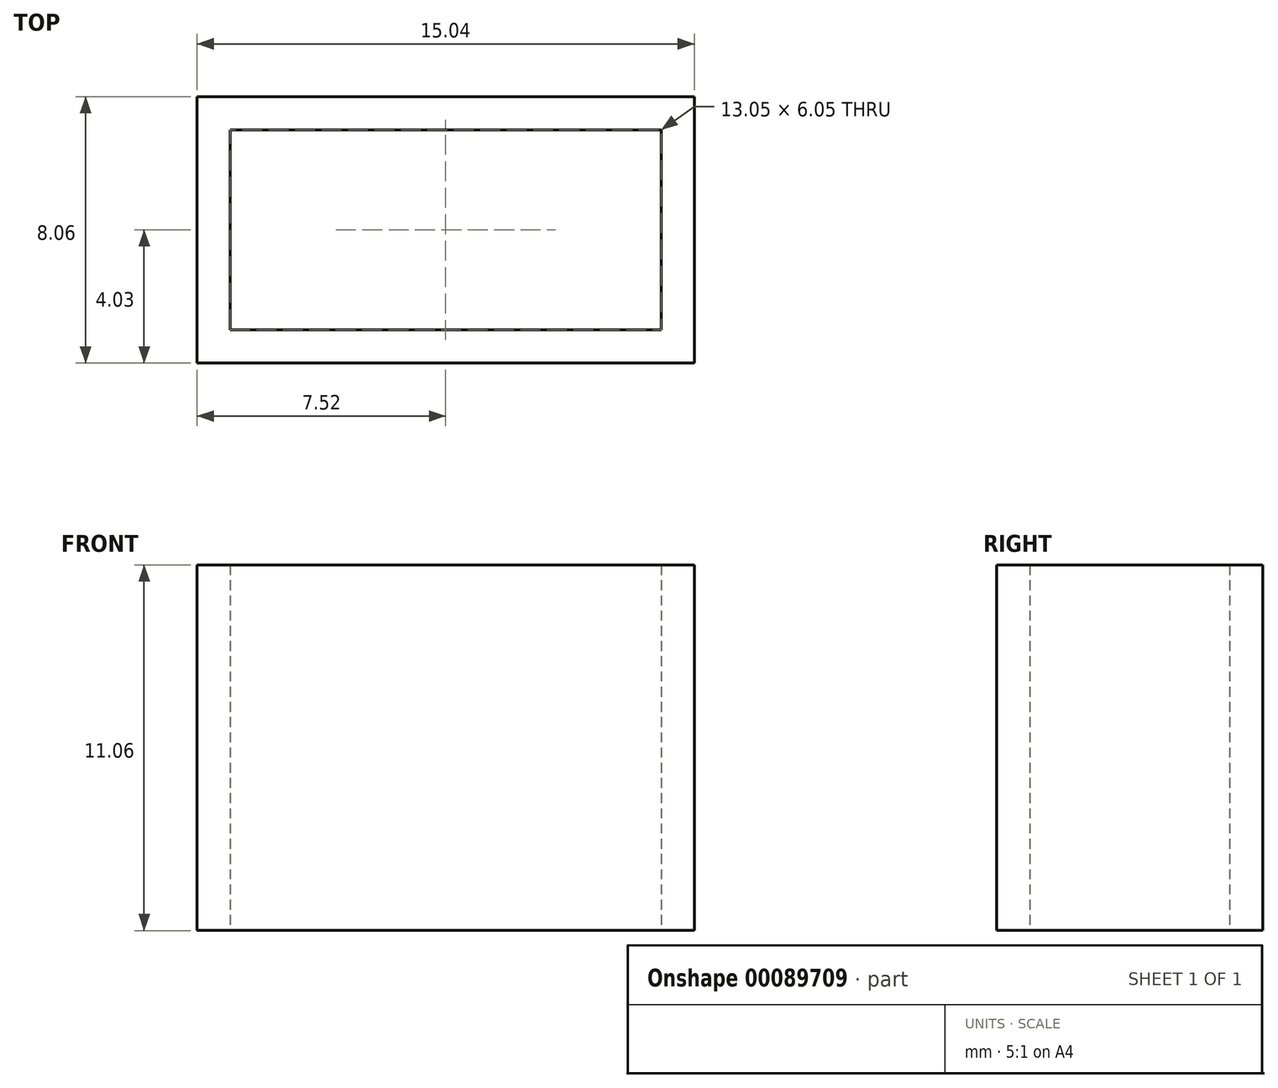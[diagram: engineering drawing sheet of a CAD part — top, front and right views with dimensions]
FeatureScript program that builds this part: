
annotation { "Feature Type Name" : "Feature", "Feature Type Description" : "" }
export const myFeature = defineFeature(function(context is Context, id is Id, definition is map)
    precondition{}
    {
        {
            var Q0;
            Q0=qCreatedBy(makeId("Top.planeOp"),FACE);
            var sketch = newSketch(context, id + "F0", { "sketchPlane" : qUnion([Q0])});
            skLineSegment(sketch, "E0.bottom", {"start": v(6.53, 3.03) * mm, "end": v(-6.53, 3.02) * mm});
            skLineSegment(sketch, "E0.top", {"start": v(6.53, -3.02) * mm, "end": v(-6.53, -3.03) * mm});
            skLineSegment(sketch, "E0.left", {"start": v(6.53, 3.03) * mm, "end": v(6.53, -3.02) * mm});
            skLineSegment(sketch, "E0.right", {"start": v(-6.53, 3.02) * mm, "end": v(-6.53, -3.03) * mm});
            skPoint(sketch, "E0.middle", {"position": v(0, 0) * mm});
            skLineSegment(sketch, "E1.bottom", {"start": v(7.53, 4.03) * mm, "end": v(-7.53, 4.03) * mm});
            skLineSegment(sketch, "E1.top", {"start": v(7.53, -4.03) * mm, "end": v(-7.53, -4.03) * mm});
            skLineSegment(sketch, "E1.left", {"start": v(7.53, 4.03) * mm, "end": v(7.53, -4.03) * mm});
            skLineSegment(sketch, "E1.right", {"start": v(-7.53, 4.03) * mm, "end": v(-7.53, -4.03) * mm});
            skSolve(sketch);
        }
        {
            var Q0;
            Q0=makeQuery(id+"F0.imprint","IMPRINT",FACE,{"disambiguationData":[TD([[makeQuery(id+"F0.imprint","IMPRINT",EDGE,{"derivedFrom":sQuery(id+"F0.wireOp",EDGE,"E0.bottom")}),-1.0]])]});
            extrude(context, id + "F1", {"entities" : qUnion([Q0]), "endBound" : BoundingType.SYMMETRIC, "depth" : 11.05 * mm});
        }
    });
